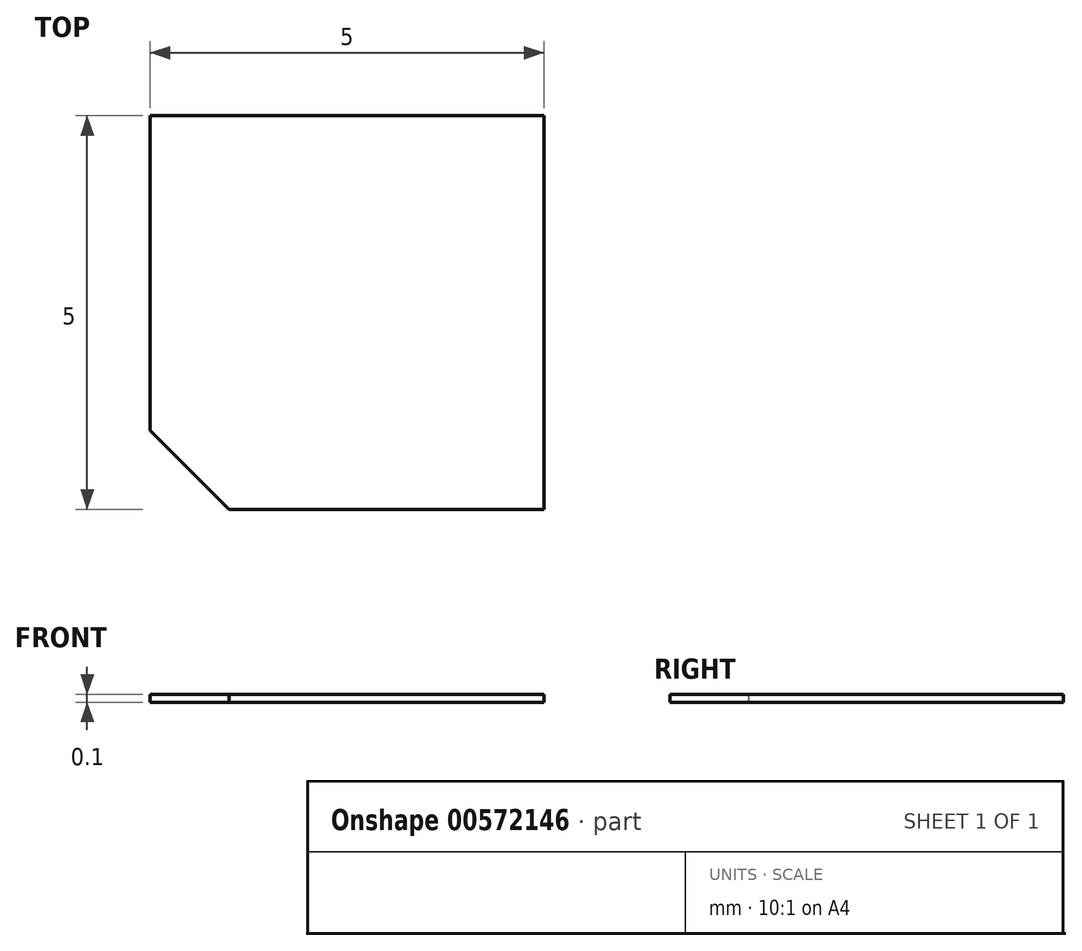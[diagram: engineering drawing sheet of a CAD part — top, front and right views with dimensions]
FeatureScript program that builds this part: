
annotation { "Feature Type Name" : "Feature", "Feature Type Description" : "" }
export const myFeature = defineFeature(function(context is Context, id is Id, definition is map)
    precondition{}
    {
        {
            var Q0;
            Q0=qCreatedBy(makeId("Top.planeOp"),FACE);
            var sketch = newSketch(context, id + "F0", { "sketchPlane" : qUnion([Q0])});
            skLineSegment(sketch, "E0", {"start": v(0, 0) * mm, "end": v(5, 0) * mm});
            skLineSegment(sketch, "E1", {"start": v(5, 0) * mm, "end": v(5, -5) * mm});
            skLineSegment(sketch, "E2", {"start": v(0, 0) * mm, "end": v(0, -4) * mm});
            skLineSegment(sketch, "E3", {"start": v(5, -5) * mm, "end": v(1, -5) * mm});
            skLineSegment(sketch, "E4", {"start": v(0, -4) * mm, "end": v(1, -5) * mm});
            skSolve(sketch);
        }
        {
            var Q0;
            Q0=makeQuery(id+"F0.imprint","IMPRINT",FACE,{"disambiguationData":[TD([[makeQuery(id+"F0.imprint","IMPRINT",EDGE,{"derivedFrom":sQuery(id+"F0.wireOp",EDGE,"E0")}),-1.0]])]});
            extrude(context, id + "F1", {"entities" : qUnion([Q0]), "depth" : 0.1 * mm, "offsetDistance" : 25 * mm});
        }
    });
